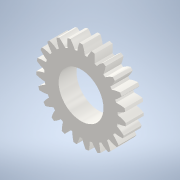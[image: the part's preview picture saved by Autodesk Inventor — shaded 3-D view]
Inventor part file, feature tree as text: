
AUTODESK INVENTOR PART (.ipt)
format: ipt  version: 2021 (Build 250183000, 183)  size: 245,248 bytes
history: native  units: mm (DEFAULTED — no unit token found)
features: plane x3, other x3, sketch x3, extrude x2
ambient origin geometry x8: Origin, YZ Plane, XZ Plane, XY Plane, X Axis, Y Axis, Z Axis, Center Point
bodies: Solid1 (feature_tree)
feature tree (11):
  extrude  "Extrusion1"  Depth=10.0mm TaperAngle=0.0deg
  plane  "Work Plane2"
  plane  "Work Plane8"
  plane  "Work Plane9"
  other  "Spur Gear"
  extrude  "Extrusion2"  Depth=10.0mm TaperAngle=0.0deg
  sketch  "Sketch1"  dims[d0=67.5mm d1=10.0mm d2=0.0mm]
  sketch  "Sketch2"  dims[d3=57.5mm d4=10.0mm d5=0.0mm]
  other  "Srf1"
  sketch  "Sketch3"  dims[d16=60.0mm d17=0.0mm d34=1.36591mm d39=0.0mm d41=0.0mm d43=60.0mm d46=60.0mm d47=0.0mm d48=0.0mm d49=25.0mm d50=10.0mm d51=0.0mm]
  other  "Pitch Diameter"
